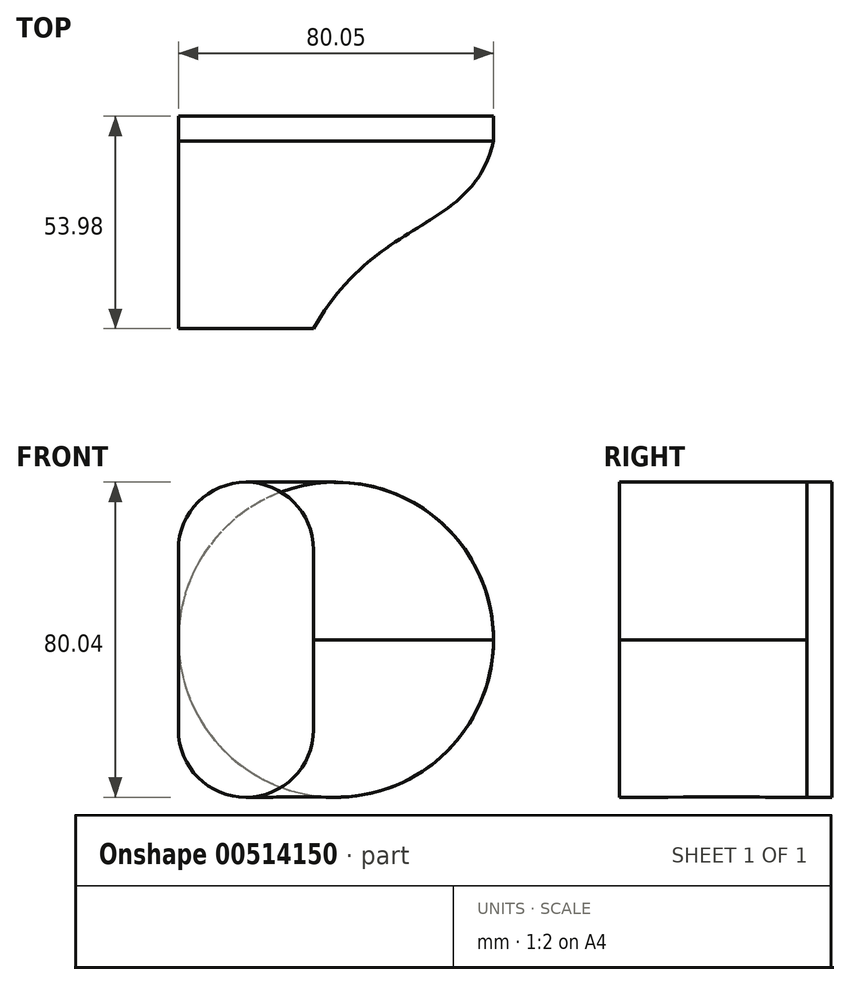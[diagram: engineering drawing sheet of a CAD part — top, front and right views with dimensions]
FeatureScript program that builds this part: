
annotation { "Feature Type Name" : "Feature", "Feature Type Description" : "" }
export const myFeature = defineFeature(function(context is Context, id is Id, definition is map)
    precondition{}
    {
        {
            var Q0;
            Q0=qCreatedBy(makeId("Front.planeOp"),FACE);
            var sketch = newSketch(context, id + "F0", { "sketchPlane" : qUnion([Q0])});
            skArc(sketch, "E0", {"start": v(-31.55, 24.62) * mm, "mid": v(-40, -1.16) * mm, "end": v(-30.07, -26.4) * mm});
            skArc(sketch, "E1", {"start": v(-30.07, -26.4) * mm, "mid": v(-0.35, -40.02) * mm, "end": v(29.6, -26.92) * mm});
            skArc(sketch, "E2", {"start": v(29.6, -26.92) * mm, "mid": v(39.97, -1.93) * mm, "end": v(32.06, 23.95) * mm});
            skArc(sketch, "E3", {"start": v(32.06, 23.95) * mm, "mid": v(0.42, 40.02) * mm, "end": v(-31.55, 24.62) * mm});
            skSolve(sketch);
        }
        {
            var Q0;
            Q0=qCreatedBy(makeId("Front.planeOp"),FACE);
            cPlane(context, id + "F1", {"entities" : qUnion([Q0]), "cplaneType" : CPlaneType.OFFSET, "offset" : 50.8 * mm, "width" : 152.4 * mm, "height" : 152.4 * mm});
        }
        {
            var Q0;
            Q0=qCreatedBy(id+"F1.planeOp",FACE);
            var sketch = newSketch(context, id + "F2", { "sketchPlane" : qUnion([Q0])});
            skLineSegment(sketch, "E4.bottom", {"start": v(-5.69, 22.85) * mm, "end": v(-40.03, 22.85) * mm, "construction": true});
            skLineSegment(sketch, "E4.top", {"start": v(-5.69, -22.85) * mm, "end": v(-40.03, -22.85) * mm, "construction": true});
            skLineSegment(sketch, "E4.left", {"start": v(-5.69, 22.85) * mm, "end": v(-5.69, -22.85) * mm});
            skLineSegment(sketch, "E4.right", {"start": v(-40.03, 22.85) * mm, "end": v(-40.03, -22.85) * mm});
            skPoint(sketch, "E4.middle", {"position": v(-22.86, 0) * mm});
            skArc(sketch, "E5", {"start": v(-5.69, 22.85) * mm, "mid": v(-22.86, 40.02) * mm, "end": v(-40.03, 22.85) * mm});
            skArc(sketch, "E6", {"start": v(-40.03, -22.85) * mm, "mid": v(-22.86, -40.02) * mm, "end": v(-5.69, -22.85) * mm});
            skLineSegment(sketch, "E7", {"start": v(-22.86, 40.02) * mm, "end": v(-22.86, -40.02) * mm, "construction": true});
            skSolve(sketch);
        }
        {
            var Q0;
            Q0 = qSketchRegion(id + "F0", true);
            extrude(context, id + "F3", {"entities" : qUnion([Q0]), "endBound" : BoundingType.SYMMETRIC, "depth" : 6.35 * mm});
        }
        {
            var Q0;
            Q0=makeQuery(id+"F3.opExtrude","CAP_FACE",FACE,{"disambiguationData":[OSD([sQuery(id+"F0.wireOp",EDGE,"E0"),sQuery(id+"F0.wireOp",EDGE,"E1"),sQuery(id+"F0.wireOp",EDGE,"E2"),sQuery(id+"F0.wireOp",EDGE,"E3")])],"isStart":false});
            var sketch = newSketch(context, id + "F4", { "sketchPlane" : qUnion([Q0])});
            skArc(sketch, "E8", {"start": v(28.52, 28.07) * mm, "mid": v(15.22, 37) * mm, "end": v(-0.52, 40.01) * mm});
            skArc(sketch, "E9", {"start": v(-33.15, 22.42) * mm, "mid": v(-40.02, -0.35) * mm, "end": v(-32.75, -23) * mm});
            skArc(sketch, "E10", {"start": v(-32.75, -23) * mm, "mid": v(-17, -36.23) * mm, "end": v(3.27, -39.88) * mm});
            skArc(sketch, "E11", {"start": v(30.86, -25.47) * mm, "mid": v(37.65, -13.55) * mm, "end": v(40.02, -0.04) * mm});
            skArc(sketch, "E12", {"start": v(-0.52, 40.01) * mm, "mid": v(-19, 35.22) * mm, "end": v(-33.15, 22.42) * mm});
            skArc(sketch, "E13", {"start": v(3.27, -39.88) * mm, "mid": v(18.52, -35.47) * mm, "end": v(30.86, -25.47) * mm});
            skArc(sketch, "E14", {"start": v(40.02, -0.04) * mm, "mid": v(37.04, 15.15) * mm, "end": v(28.52, 28.07) * mm});
            skSolve(sketch);
        }
        {
            var Q0;
            Q0=qCreatedBy(makeId("Top.planeOp"),FACE);
            var sketch = newSketch(context, id + "F5", { "sketchPlane" : qUnion([Q0])});
            skFitSpline(sketch, "E15", {"points": [v(40.02, -3.18) * mm, v(-5.69, -50.8) * mm], "startDerivative": vector(-16, -69.52) * mm, "endDerivative": vector(-47.77, -85.89) * mm});
            skLineSegment(sketch, "E16", {"start": v(-40.03, -50.8) * mm, "end": v(-40.02, -3.17) * mm});
            skSolve(sketch);
        }
        {
            var Q0;
            Q0 = qSketchRegion(id + "F2", true);
            var Q1;
            Q1 = qSketchRegion(id + "F4", true);
            var Q2;
            Q2=sQuery(id+"F5.wireOp",EDGE,"E15");
            var Q3;
            Q3=sQuery(id+"F5.wireOp",EDGE,"E16");
            var Q4;
            Q4=sQuery(id+"F2.wireOp",VERTEX,"E4.left.end");
            var Q5;
            Q5=sQuery(id+"F4.wireOp",VERTEX,"E13.end");
            loft(context, id + "F6", {"addGuides" : true, "sheetProfilesArray" : [{ "sheetProfileEntities" : qUnion([Q0]) }, { "sheetProfileEntities" : qUnion([Q1]) }], "guidesArray" : [{ "guideEntities" : qUnion([Q2]), "guideDerivativeType" : LoftGuideDerivativeType.DEFAULT, "guideDerivativeMagnitude" : 1 }, { "guideEntities" : qUnion([Q3]), "guideDerivativeType" : LoftGuideDerivativeType.DEFAULT, "guideDerivativeMagnitude" : 1 }], "matchConnections" : true, "connections" : [{ "connectionEntities" : qUnion([Q4, Q5]), "connectionEdgeQueries" : qUnion([]), "connectionEdgeParameters" : [] }]});
        }
    });
